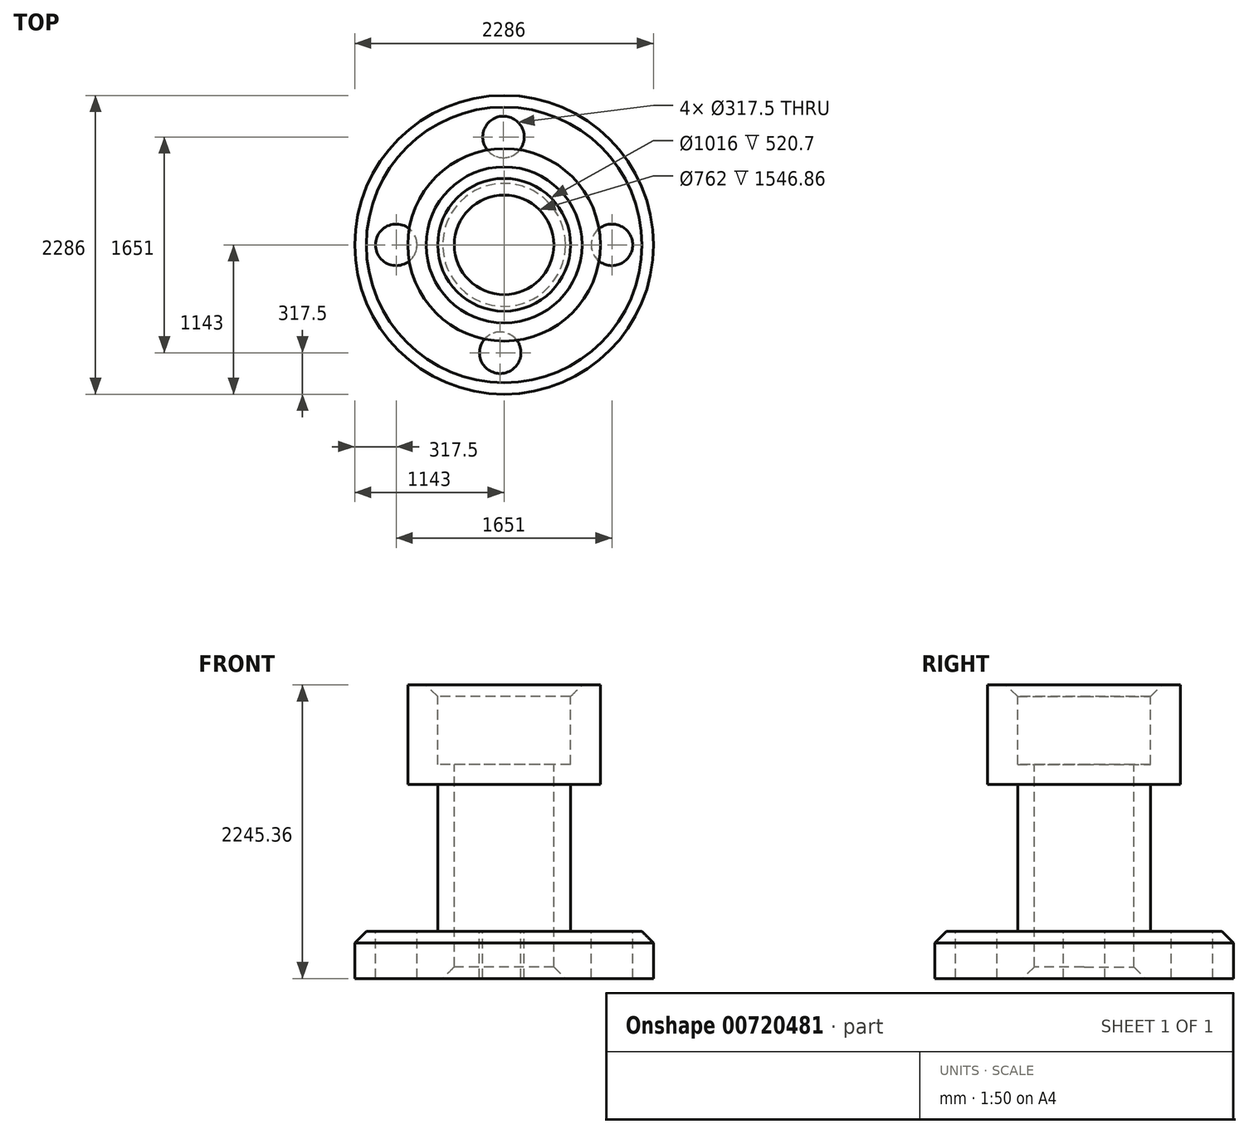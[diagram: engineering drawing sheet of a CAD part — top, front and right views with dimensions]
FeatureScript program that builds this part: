
annotation { "Feature Type Name" : "Feature", "Feature Type Description" : "" }
export const myFeature = defineFeature(function(context is Context, id is Id, definition is map)
    precondition{}
    {
        {
            var Q0;
            Q0=qCreatedBy(makeId("Front.planeOp"),FACE);
            var sketch = newSketch(context, id + "F0", { "sketchPlane" : qUnion([Q0])});
            skLineSegment(sketch, "E0", {"start": v(0, 0) * mm, "end": v(228.88, 0) * mm});
            skLineSegment(sketch, "E1", {"start": v(228.88, 0) * mm, "end": v(228.88, -762) * mm});
            skLineSegment(sketch, "E2", {"start": v(228.88, -762) * mm, "end": v(0, -762) * mm});
            skLineSegment(sketch, "E3", {"start": v(0, -762) * mm, "end": v(0, -1884.68) * mm});
            skLineSegment(sketch, "E4", {"start": v(0, -1884.68) * mm, "end": v(635, -1884.68) * mm});
            skLineSegment(sketch, "E5", {"start": v(635, -1884.68) * mm, "end": v(635, -2245.36) * mm});
            skLineSegment(sketch, "E6", {"start": v(635, -2245.36) * mm, "end": v(-127, -2245.36) * mm});
            skLineSegment(sketch, "E7", {"start": v(-127, -2245.36) * mm, "end": v(-127, -609.6) * mm});
            skLineSegment(sketch, "E8", {"start": v(-127, -609.6) * mm, "end": v(0, -609.6) * mm});
            skLineSegment(sketch, "E9", {"start": v(0, -609.6) * mm, "end": v(0, 0) * mm});
            skLineSegment(sketch, "E10", {"start": v(-508, -564.43) * mm, "end": v(-508, -1208.18) * mm});
            skSolve(sketch);
        }
        {
            var Q0;
            Q0 = qSketchRegion(id + "F0", true);
            var Q1;
            Q1=sQuery(id+"F0.wireOp",EDGE,"E10");
            revolve(context, id + "F1", {"surfaceOperationType" : NewSurfaceOperationType.NEW, "entities" : qUnion([Q0]), "axis" : qUnion([Q1]), "revolveType" : RevolveType.FULL});
        }
        {
            var Q0;
            Q0=makeQuery(id+"F1.opRevolve","SWEPT_FACE",FACE,{"disambiguationData":[OSD([sQuery(id+"F0.wireOp",EDGE,"E4")])]});
            var sketch = newSketch(context, id + "F2", { "sketchPlane" : qUnion([Q0])});
            skPoint(sketch, "E11", {"position": v(-508, 0) * mm});
            skCircle(sketch, "E12", {"center": v(-512.9, 825.5) * mm, "radius": 158.75 * mm});
            skCircle(sketch, "E13", {"center": v(317.5, 0) * mm, "radius": 158.75 * mm});
            skCircle(sketch, "E14", {"center": v(-537.74, -825.5) * mm, "radius": 158.75 * mm});
            skCircle(sketch, "E15", {"center": v(-1333.5, 0) * mm, "radius": 158.75 * mm});
            skSolve(sketch);
        }
        {
            var Q0;
            Q0=makeQuery(id+"F2.imprint","IMPRINT",FACE,{"disambiguationData":[TD([[makeQuery(id+"F2.imprint","IMPRINT",EDGE,{"derivedFrom":sQuery(id+"F2.wireOp",EDGE,"E15")}),1.0]])]});
            extrude(context, id + "F3", {"entities" : qUnion([Q0]), "operationType" : NewBodyOperationType.REMOVE, "oppositeDirection" : true, "depth" : 360.68 * mm, "offsetDistance" : 25.4 * mm});
        }
        {
            var Q0;
            Q0=makeQuery(id+"F2.imprint","IMPRINT",FACE,{"disambiguationData":[TD([[makeQuery(id+"F2.imprint","IMPRINT",EDGE,{"derivedFrom":sQuery(id+"F2.wireOp",EDGE,"E14")}),1.0]])]});
            extrude(context, id + "F4", {"entities" : qUnion([Q0]), "operationType" : NewBodyOperationType.REMOVE, "oppositeDirection" : true, "depth" : 360.68 * mm, "offsetDistance" : 25.4 * mm});
        }
        {
            var Q0;
            Q0=makeQuery(id+"F2.imprint","IMPRINT",FACE,{"disambiguationData":[TD([[makeQuery(id+"F2.imprint","IMPRINT",EDGE,{"derivedFrom":sQuery(id+"F2.wireOp",EDGE,"E13")}),1.0]])]});
            extrude(context, id + "F5", {"entities" : qUnion([Q0]), "operationType" : NewBodyOperationType.REMOVE, "oppositeDirection" : true, "depth" : 360.68 * mm, "offsetDistance" : 25.4 * mm});
        }
        {
            var Q0;
            Q0=makeQuery(id+"F2.imprint","IMPRINT",FACE,{"disambiguationData":[TD([[makeQuery(id+"F2.imprint","IMPRINT",EDGE,{"derivedFrom":sQuery(id+"F2.wireOp",EDGE,"E12")}),1.0]])]});
            extrude(context, id + "F6", {"entities" : qUnion([Q0]), "operationType" : NewBodyOperationType.REMOVE, "oppositeDirection" : true, "depth" : 360.68 * mm, "offsetDistance" : 25.4 * mm});
        }
        {
            var Q0;
            Q0=makeQuery(id+"F1.opRevolve","SWEPT_EDGE",EDGE,{"disambiguationData":[OSD([sQuery(id+"F0.wireOp",EDGE,"E6"),sQuery(id+"F0.wireOp",EDGE,"E7")])]});
            chamfer(context, id + "F7", {"entities" : qUnion([Q0]), "width" : 88.9 * mm, "tangentPropagation" : true});
        }
        {
            var Q0;
            Q0=makeQuery(id+"F1.opRevolve","SWEPT_EDGE",EDGE,{"disambiguationData":[OSD([sQuery(id+"F0.wireOp",EDGE,"E0"),sQuery(id+"F0.wireOp",EDGE,"E9")])]});
            chamfer(context, id + "F8", {"entities" : qUnion([Q0]), "width" : 88.9 * mm, "tangentPropagation" : true});
        }
        {
            var Q0;
            Q0=makeQuery(id+"F1.opRevolve","SWEPT_EDGE",EDGE,{"disambiguationData":[OSD([sQuery(id+"F0.wireOp",EDGE,"E4"),sQuery(id+"F0.wireOp",EDGE,"E5")])]});
            chamfer(context, id + "F9", {"entities" : qUnion([Q0]), "width" : 88.9 * mm, "tangentPropagation" : true});
        }
    });
